# Revit family: Tinka 15W
name_source: partatom
category: Lighting Fixtures
revit_build: Autodesk Revit 2015 (Build: 20140322_1515(x64)
units: mm (PartAtom-declared; Revit-internal decimal feet)

## types (2) — shared parameters
Beam Angle = 25°
CRI = 82
Casing Color = White
Cutout = -
Default Elevation = 1219 mm
Depth = -
Description = Tracklight, 3-Circuit Track
Dimensions = 90mm x 238mm
Dimmable = Yes
Directivity = Yes
Driver = Integrated
Housing Material = Aluminium
IP Code = IP20
Lamp = LED
Last Updated = 2.3.2017
Lifetime L70 = 50000h
Manufacturer = Winled Oy Ltd
Model = Tinka 15W
Operating Temperature Range = -20° to +50°C
Type Image = Tinka 15W.png
URL = www.winled.fi
Voltage = 230 V
Wattage Comments = 15W

## per-type parameters (varying)
| type | Color Temperature | Light source | Lumens Output | Product Number |
| Tinka 15W, Neutral White, 230V - 53ER997N015E | 4000K | Tinka light NV | 1227lm | 53ER997N015E |
| Tinka 15W, Warm White, 230V - 53ER997L015E | 3000K | Tinka light LV | 1172lm | 53ER997L015E |

## geometry (parser evidence)
native form markers: Sweep x16
no freeform markers — native parametric forms only
